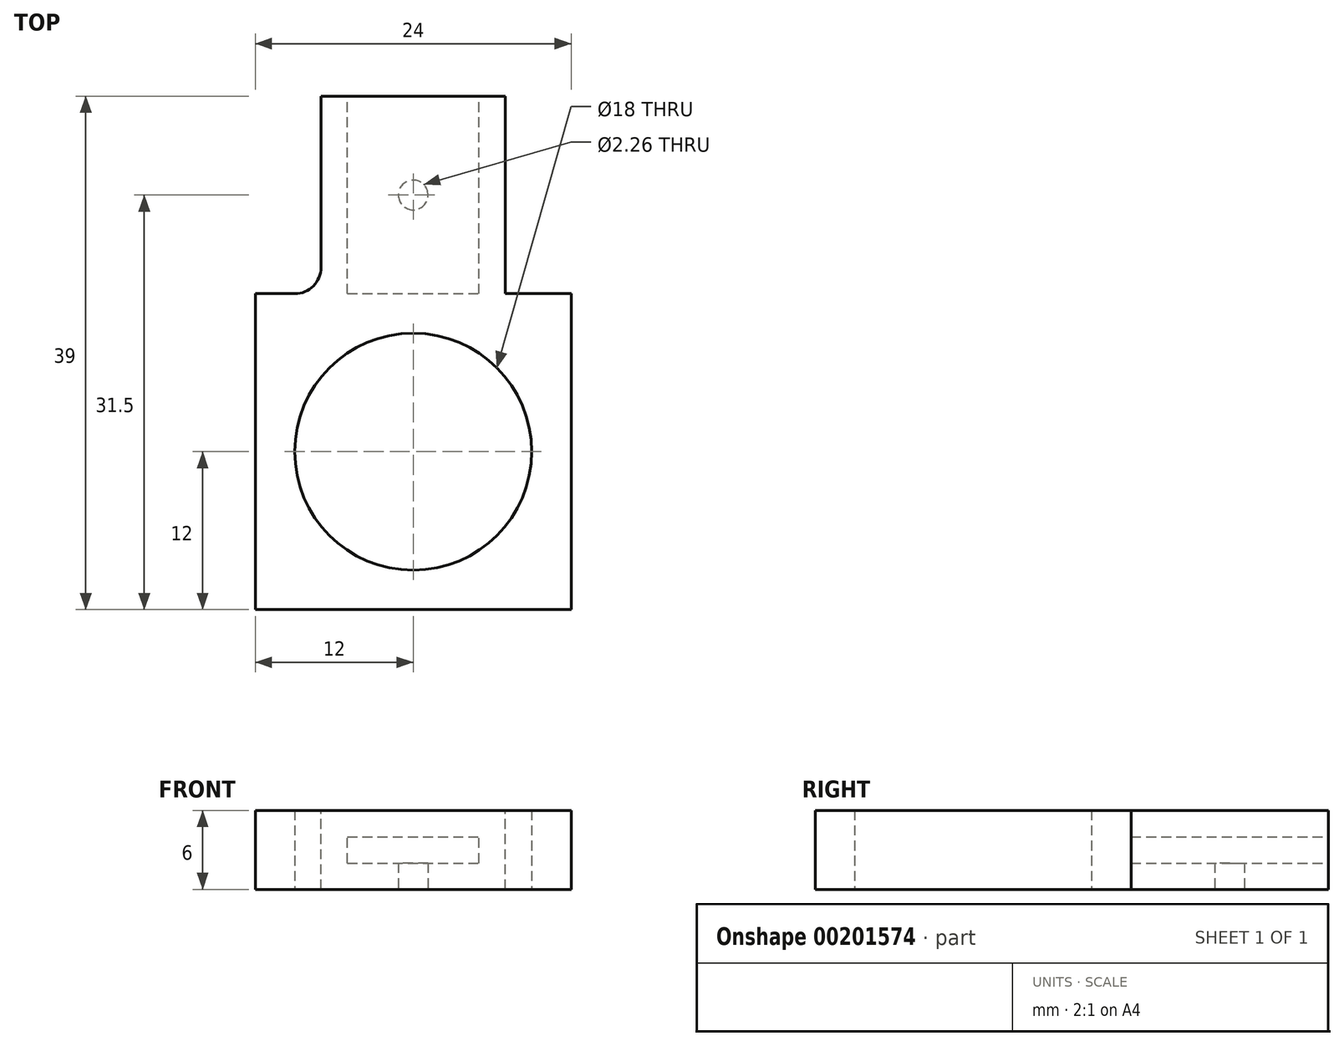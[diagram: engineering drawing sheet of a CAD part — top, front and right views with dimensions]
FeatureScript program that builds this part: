
annotation { "Feature Type Name" : "Feature", "Feature Type Description" : "" }
export const myFeature = defineFeature(function(context is Context, id is Id, definition is map)
    precondition{}
    {
        {
            var Q0;
            Q0=qCreatedBy(makeId("Front.planeOp"),FACE);
            var sketch = newSketch(context, id + "F0", { "sketchPlane" : qUnion([Q0])});
            skLineSegment(sketch, "E0.bottom", {"start": v(-5, 0) * mm, "end": v(5, 0) * mm});
            skLineSegment(sketch, "E0.top", {"start": v(-5, 2) * mm, "end": v(5, 2) * mm});
            skLineSegment(sketch, "E0.left", {"start": v(-5, 0) * mm, "end": v(-5, 2) * mm});
            skLineSegment(sketch, "E0.right", {"start": v(5, 0) * mm, "end": v(5, 2) * mm});
            skLineSegment(sketch, "E1.0", {"start": v(-7, 4) * mm, "end": v(7, 4) * mm});
            skLineSegment(sketch, "E1.1", {"start": v(-7, -2) * mm, "end": v(-7, 4) * mm});
            skLineSegment(sketch, "E1.2", {"start": v(-7, -2) * mm, "end": v(7, -2) * mm});
            skLineSegment(sketch, "E1.3", {"start": v(7, -2) * mm, "end": v(7, 4) * mm});
            skSolve(sketch);
        }
        {
            var Q0;
            Q0=makeQuery(id+"F0.imprint","IMPRINT",FACE,{"disambiguationData":[TD([[makeQuery(id+"F0.imprint","IMPRINT",EDGE,{"derivedFrom":sQuery(id+"F0.wireOp",EDGE,"E0.bottom")}),-1.0]])]});
            extrude(context, id + "F1", {"entities" : qUnion([Q0]), "depth" : 15 * mm});
        }
        {
            var Q0;
            Q0=qCreatedBy(makeId("Top.planeOp"),FACE);
            var sketch = newSketch(context, id + "F2", { "sketchPlane" : qUnion([Q0])});
            skLineSegment(sketch, "E2.bottom", {"start": v(-12, -15) * mm, "end": v(12, -15) * mm});
            skLineSegment(sketch, "E2.top", {"start": v(-12, -39) * mm, "end": v(12, -39) * mm});
            skLineSegment(sketch, "E2.left", {"start": v(-12, -15) * mm, "end": v(-12, -39) * mm});
            skLineSegment(sketch, "E2.right", {"start": v(12, -15) * mm, "end": v(12, -39) * mm});
            skPoint(sketch, "E3", {"position": v(0, -27) * mm});
            skSolve(sketch);
        }
        {
            var Q0;
            Q0 = qSketchRegion(id + "F2", true);
            var Q1;
            Q1=makeQuery(id+"F1.opExtrude","SWEPT_FACE",FACE,{"disambiguationData":[OSD([sQuery(id+"F0.wireOp",EDGE,"E1.0")])]});
            var Q2;
            Q2=makeQuery(id+"F1.opExtrude","SWEPT_FACE",FACE,{"disambiguationData":[OSD([sQuery(id+"F0.wireOp",EDGE,"E1.2")])]});
            extrude(context, id + "F3", {"entities" : qUnion([Q0]), "operationType" : NewBodyOperationType.ADD, "endBound" : BoundingType.UP_TO_SURFACE, "endBoundEntityFace" : qUnion([Q1]), "depth" : 25 * mm, "hasSecondDirection" : true, "secondDirectionBound" : SecondDirectionBoundingType.UP_TO_SURFACE, "secondDirectionOppositeDirection" : true, "secondDirectionBoundEntityFace" : qUnion([Q2]), "secondDirectionDepth" : 25 * mm});
        }
        {
            var Q0;
            {var subQ0=sQuery(id+"F0.wireOp",EDGE,"E1.2");Q0=makeQuery(id+"F3.boolean.opBoolean","MERGE",FACE,{"derivedFrom":[makeQuery(id+"F1.opExtrude","SWEPT_FACE",FACE,{"disambiguationData":[OSD([subQ0])]}),makeQuery(id+"F3.opExtrude","CAP_FACE",FACE,{"disambiguationData":[OSD([subQ0])],"isStart":true})]});}
            var sketch = newSketch(context, id + "F4", { "sketchPlane" : qUnion([Q0])});
            skPoint(sketch, "E4.0", {"position": v(0, 27) * mm});
            skPoint(sketch, "E5", {"position": v(0, 7.5) * mm});
            skSolve(sketch);
        }
        {
            var Q0;
            Q0=sQuery(id+"F4.wireOp",VERTEX,"E4.0");
            var Q1;
            Q1=makeQuery(id+"F1.opExtrude","SWEPT_BODY",BODY,{"disambiguationData":[OSD([sQuery(id+"F0.wireOp",EDGE,"E0.bottom"),sQuery(id+"F0.wireOp",EDGE,"E0.top"),sQuery(id+"F0.wireOp",EDGE,"E0.left"),sQuery(id+"F0.wireOp",EDGE,"E0.right"),sQuery(id+"F0.wireOp",EDGE,"E1.0"),sQuery(id+"F0.wireOp",EDGE,"E1.1"),sQuery(id+"F0.wireOp",EDGE,"E1.2"),sQuery(id+"F0.wireOp",EDGE,"E1.3")])]});
            hole(context, id + "F5", {"style" : HoleStyle.SIMPLE, "endStyle" : HoleEndStyle.THROUGH, "holeDiameter" : 18 * mm, "locations" : qUnion([Q0]), "scope" : qUnion([Q1]), "isTappedThrough" : true});
        }
        {
            var Q0;
            Q0=makeQuery(id+"F3.opExtrude","TWEAK_EDGE",EDGE,{"derivedFrom":[makeQuery(id+"F2.imprint","IMPRINT",EDGE,{"derivedFrom":sQuery(id+"F2.wireOp",EDGE,"E2.top")}),makeQuery(id+"F2.imprint","IMPRINT",EDGE,{"derivedFrom":sQuery(id+"F2.wireOp",EDGE,"E2.right")})]});
            var Q1;
            Q1=makeQuery(id+"F3.opExtrude","TWEAK_EDGE",EDGE,{"derivedFrom":[makeQuery(id+"F2.imprint","IMPRINT",EDGE,{"derivedFrom":sQuery(id+"F2.wireOp",EDGE,"E2.bottom")}),makeQuery(id+"F2.imprint","IMPRINT",EDGE,{"derivedFrom":sQuery(id+"F2.wireOp",EDGE,"E2.right")})]});
            var Q2;
            Q2=makeQuery(id+"F1.opExtrude","CAP_EDGE",EDGE,{"disambiguationData":[OSD([sQuery(id+"F0.wireOp",EDGE,"E1.3")])],"isStart":false});
            var Q3;
            Q3=makeQuery(id+"F3.opExtrude","TWEAK_EDGE",EDGE,{"derivedFrom":[makeQuery(id+"F2.imprint","IMPRINT",EDGE,{"derivedFrom":sQuery(id+"F2.wireOp",EDGE,"E2.top")}),makeQuery(id+"F2.imprint","IMPRINT",EDGE,{"derivedFrom":sQuery(id+"F2.wireOp",EDGE,"E2.left")})]});
            var Q4;
            Q4=makeQuery(id+"F3.opExtrude","TWEAK_EDGE",EDGE,{"derivedFrom":[makeQuery(id+"F2.imprint","IMPRINT",EDGE,{"derivedFrom":sQuery(id+"F2.wireOp",EDGE,"E2.bottom")}),makeQuery(id+"F2.imprint","IMPRINT",EDGE,{"derivedFrom":sQuery(id+"F2.wireOp",EDGE,"E2.left")})]});
            var Q5;
            Q5=makeQuery(id+"F1.opExtrude","CAP_EDGE",EDGE,{"disambiguationData":[OSD([sQuery(id+"F0.wireOp",EDGE,"E1.1")])],"isStart":false});
            fillet(context, id + "F6", {"entities" : qUnion([Q0, Q1, Q2, Q3, Q4, Q5]), "radius" : 2 * mm, "tangentPropagation" : true, "allowEdgeOverflow" : false});
        }
        {
            var Q0;
            Q0=sQuery(id+"F4.wireOp",VERTEX,"E5");
            var Q1;
            Q1=makeQuery(id+"F1.opExtrude","SWEPT_BODY",BODY,{"disambiguationData":[OSD([sQuery(id+"F0.wireOp",EDGE,"E0.bottom"),sQuery(id+"F0.wireOp",EDGE,"E0.top"),sQuery(id+"F0.wireOp",EDGE,"E0.left"),sQuery(id+"F0.wireOp",EDGE,"E0.right"),sQuery(id+"F0.wireOp",EDGE,"E1.0"),sQuery(id+"F0.wireOp",EDGE,"E1.1"),sQuery(id+"F0.wireOp",EDGE,"E1.2"),sQuery(id+"F0.wireOp",EDGE,"E1.3")])]});
            hole(context, id + "F7", {"style" : HoleStyle.SIMPLE, "endStyle" : HoleEndStyle.BLIND, "standardTappedOrClearance" : lookupTablePath({ "standard" : "ANSI", "engagement" : "75%", "pitch" : "40 tpi", "size" : "#4", "type" : "Tapped" }), "standardBlindInLast" : lookupTablePath({ "standard" : "ANSI", "engagement" : "75%", "pitch" : "40 tpi", "size" : "#4", "type" : "Tapped" }), "holeDiameter" : 2.26 * mm, "holeDepth" : 2.3 * mm, "locations" : qUnion([Q0]), "scope" : qUnion([Q1]), "majorDiameter" : 2.84 * mm});
        }
    });
